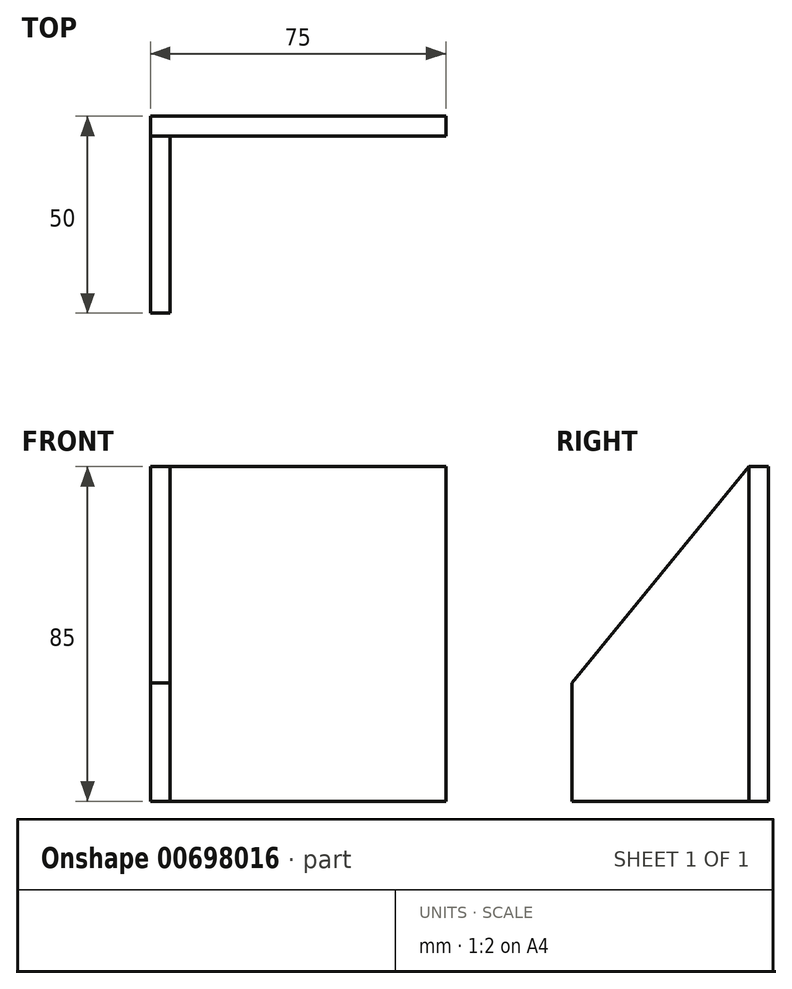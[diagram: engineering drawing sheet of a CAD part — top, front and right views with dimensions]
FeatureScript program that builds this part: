
annotation { "Feature Type Name" : "Feature", "Feature Type Description" : "" }
export const myFeature = defineFeature(function(context is Context, id is Id, definition is map)
    precondition{}
    {
        {
            var Q0;
            Q0=qCreatedBy(makeId("Front.planeOp"),FACE);
            var sketch = newSketch(context, id + "F0", { "sketchPlane" : qUnion([Q0])});
            skLineSegment(sketch, "E0.bottom", {"start": v(0, 0) * mm, "end": v(75, 0) * mm});
            skLineSegment(sketch, "E0.top", {"start": v(0, 85) * mm, "end": v(75, 85) * mm});
            skLineSegment(sketch, "E0.left", {"start": v(0, 0) * mm, "end": v(0, 85) * mm});
            skLineSegment(sketch, "E0.right", {"start": v(75, 0) * mm, "end": v(75, 85) * mm});
            skSolve(sketch);
        }
        {
            var Q0;
            Q0=makeQuery(id+"F0.imprint","IMPRINT",FACE,{"disambiguationData":[TD([[makeQuery(id+"F0.imprint","IMPRINT",EDGE,{"derivedFrom":sQuery(id+"F0.wireOp",EDGE,"E0.bottom")}),1.0]])]});
            extrude(context, id + "F1", {"entities" : qUnion([Q0]), "depth" : 5 * mm, "offsetDistance" : 25 * mm});
        }
        {
            var Q0;
            Q0=makeQuery(id+"F1.opExtrude","SWEPT_FACE",FACE,{"disambiguationData":[OSD([sQuery(id+"F0.wireOp",EDGE,"E0.left")])]});
            var sketch = newSketch(context, id + "F2", { "sketchPlane" : qUnion([Q0])});
            skLineSegment(sketch, "E1", {"start": v(5, 0) * mm, "end": v(50, 0) * mm});
            skLineSegment(sketch, "E2", {"start": v(50, 0) * mm, "end": v(50, 30) * mm});
            skLineSegment(sketch, "E3", {"start": v(50, 30) * mm, "end": v(5, 85) * mm});
            skLineSegment(sketch, "E4", {"start": v(5, 85) * mm, "end": v(5, 0) * mm});
            skSolve(sketch);
        }
        {
            var Q0;
            Q0=makeQuery(id+"F2.imprint","IMPRINT",FACE,{"disambiguationData":[TD([[makeQuery(id+"F2.imprint","IMPRINT",EDGE,{"derivedFrom":sQuery(id+"F2.wireOp",EDGE,"E1")}),1.0]])]});
            extrude(context, id + "F3", {"entities" : qUnion([Q0]), "oppositeDirection" : true, "depth" : 5 * mm, "offsetDistance" : 25 * mm});
        }
    });
